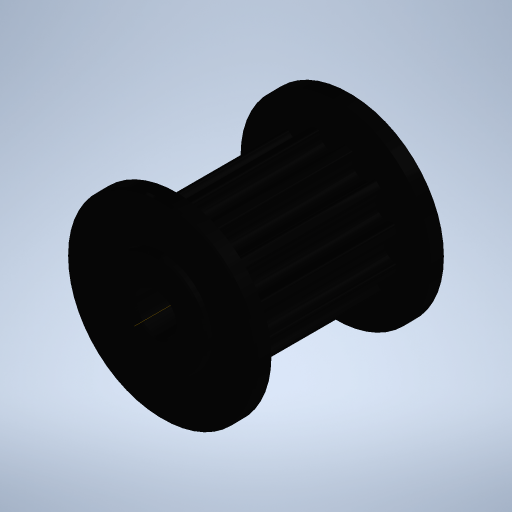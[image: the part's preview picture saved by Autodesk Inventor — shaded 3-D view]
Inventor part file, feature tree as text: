
AUTODESK INVENTOR PART (.ipt)
format: ipt  version: 2023.3 (Build 273359000, 359)  size: 313,856 bytes
history: native  units: mm (DEFAULTED — no unit token found)
features: other x1, chamfer x1
ambient origin geometry x8: Origin, YZ Plane, XZ Plane, XY Plane, X Axis, Y Axis, Z Axis, Center Point
bodies: Solid1 (feature_tree)
feature tree (2):
  other  "Work Axis1"
  chamfer  "Chamfer2"  [1 undecoded]
note: 1 required parameter value undecoded (feature->parameter linkage not recoverable at this tier; creation-order binding heuristic only, values carry confidence <= 0.55)
